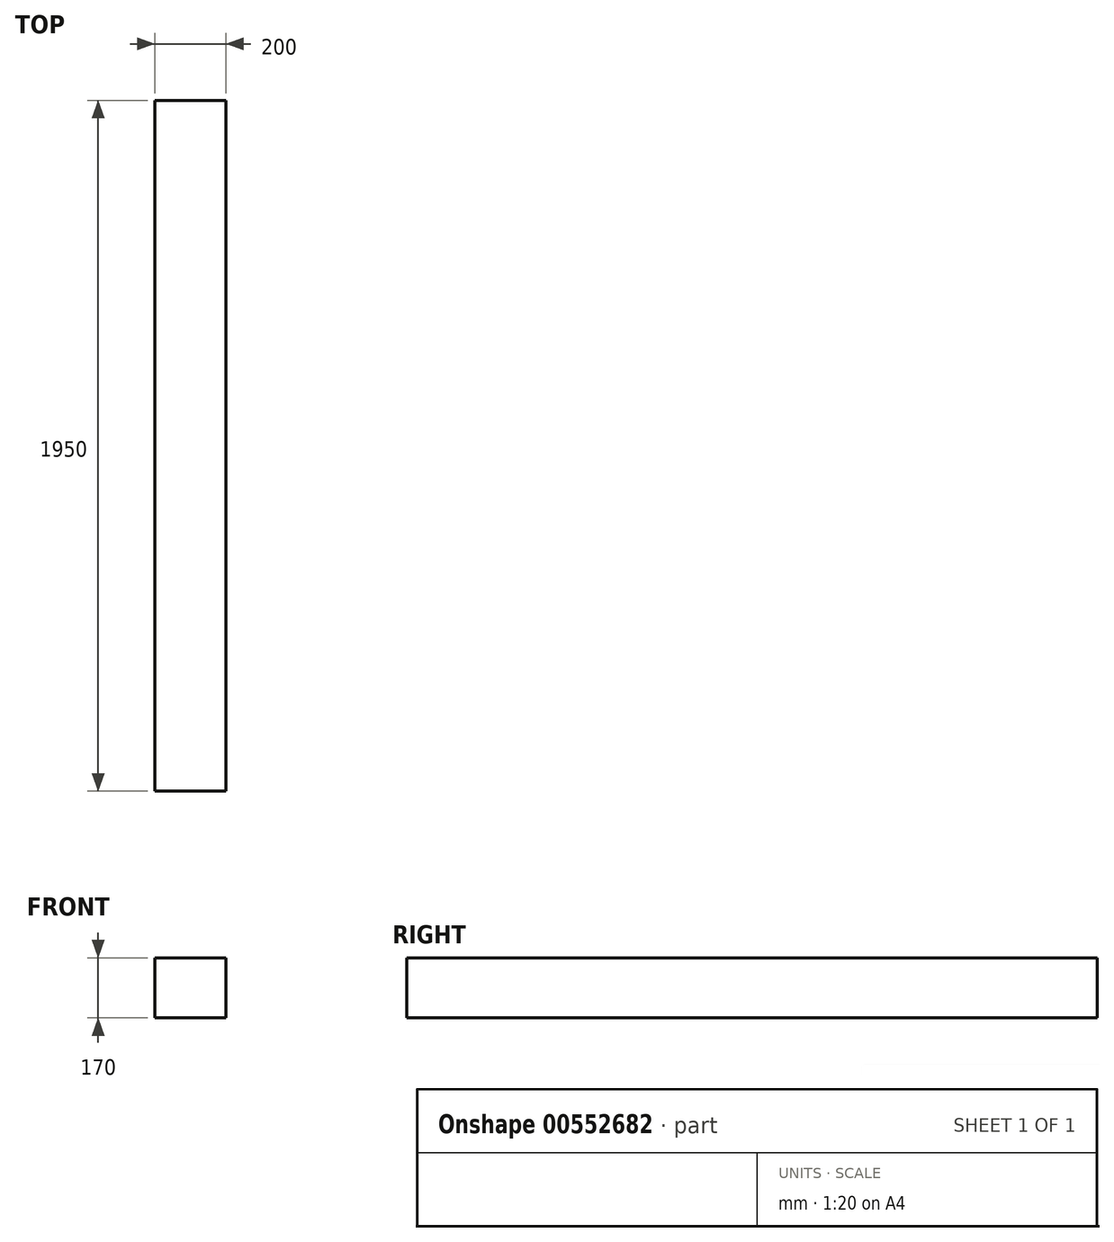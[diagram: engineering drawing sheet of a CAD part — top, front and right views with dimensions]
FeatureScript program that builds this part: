
annotation { "Feature Type Name" : "Feature", "Feature Type Description" : "" }
export const myFeature = defineFeature(function(context is Context, id is Id, definition is map)
    precondition{}
    {
        {
            var Q0;
            Q0=qCreatedBy(makeId("Front.planeOp"),FACE);
            var sketch = newSketch(context, id + "F0", { "sketchPlane" : qUnion([Q0])});
            skLineSegment(sketch, "E0.bottom", {"start": v(100, 85) * mm, "end": v(-100, 85) * mm});
            skLineSegment(sketch, "E0.top", {"start": v(100, -85) * mm, "end": v(-100, -85) * mm});
            skLineSegment(sketch, "E0.left", {"start": v(100, 85) * mm, "end": v(100, -85) * mm});
            skLineSegment(sketch, "E0.right", {"start": v(-100, 85) * mm, "end": v(-100, -85) * mm});
            skPoint(sketch, "E0.middle", {"position": v(0, 0) * mm});
            skSolve(sketch);
        }
        {
            var Q0;
            Q0 = qSketchRegion(id + "F0", true);
            extrude(context, id + "F1", {"entities" : qUnion([Q0]), "oppositeDirection" : true, "depth" : 1950 * mm, "offsetDistance" : 25 * mm});
        }
    });
